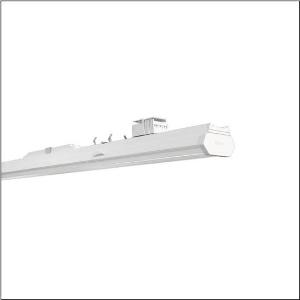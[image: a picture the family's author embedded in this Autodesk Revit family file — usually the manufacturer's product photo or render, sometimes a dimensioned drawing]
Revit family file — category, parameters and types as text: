
# Revit family: licross_r__21_protected_ho_52td1bcn4b5m_1c3e
name_source: partatom
category: Lighting Fixtures
units: mm (PartAtom-declared; Revit-internal decimal feet)

## family parameters
Cut with Voids When Loaded = No
Host = Face
Light Source = No
Part Type = Normal
Room Calculation Point = No
Round Connector Dimension = Use Diameter
Shared = No

## types (1)
- --- (1 x LED, 11820 lm, 68.9 W, 4000K)
    Apparent Load = 69 VA
    CIE Flux Codes = 54 82 95 97 100
    Color Rendering = 80
    Color Temperature = 4000K
    Default Elevation = 1800 mm
    Description = Licross® 21 Protected HO, luminaire insert, of sheet steel, galvanised, coil coated, white, length: 1.500mm, width: 90mm, height: 103mm, LED rated luminous flux: 11.830lm, light colour: 840, control gear: ON/OFF Multilumen, CLOi, control gear: ECG Multilumen, with plug, 3-pole, with phase selection, mains connection: 220..240V, AC, 50/60Hz, start of lifetime: 69W, end of service life: 83W, halogen-free wiring, primary optical cover: cover, of PMMA, light emission: direct distribution, primary light characteristic: symmetric, protection rating (complete): IP54, insulation class (complete): insulation class I (protective earthing), certification: CE, ENEC, VDE, UKCA, protection symbol: D if used in an environment with non-conductive dust loads with corresponding accessories, impact resistance: IK06, permissible ambient temperature for indoor applications: -35..+35°C, corresponds to IFS (International Featured Standards) requirements for safety and quality in the food industry, reducing of maximum allowable ambient temperature of 5°C with ceiling mounting, LABS conformity tested according to VDMA 24364:2018-05, packaging unit: 1 piece
    Height = 92 mm
    Lamp = 1 x LED
    Lamp Light Flux = 11820 lm
    Lamp Power = 68.9 W
    Lamp count = 1
    Length = 1500 mm
    Luminous efficacy = 172 lm/W
    Manufacturer = Siteco
    ModVariant = No
    Model = 52TD1BCN4B5M
    Mounting Place = Ceiling
    Mounting Type = Pendant
    Number of Poles = 1
    OnlyDefault = Yes
    Power Factor = 1
    Product Name = Licross® 21 Protected HO
    Product group = luminaire insert
    ProductGroupID = 901
    Protection Class = Protection class I
    Protection Degree = IP 54
    RLX_Detail_Level = 1
    RLX_Emergency_Light_Flux = 0 lm
    RLX_Emergency_Type = 0
    RLX_Emergency_Type_DB = No
    RlxData = <blob elided: 22069 chars, md5=05335325>
    Socket = socket
    Standby Power = 0 W
    System Light Flux = 11820 lm
    System Power = 69 W
    Type Comments = factory setting: luminous flux: 100 % | (A | C | E) | 162 mA
    Type Image = l_1256148.jpg
    URL = http://relux.com
    VarID = @adj_059775
    Voltage = 0 V
    Weight = 0.00 kg
    Width = 88 mm

## geometry (parser evidence)
native form markers: Blend x4, Sweep x10
no freeform markers — native parametric forms only
